# Revit family: Sink-Vanity_Top-Lavatory-KOHLER-MODERN_LIFE-K-77835T_1
name_source: partatom
category: Plumbing Fixtures
revit_build: Autodesk Revit 2017 (Build: 20160225_1515(x64)
units: mm (PartAtom-declared; Revit-internal decimal feet)

## family parameters
Cut with Voids When Loaded = No
Host = Face
OmniClass Number = 23.31.13.00
OmniClass Title = Sinks
Part Type = Normal
Room Calculation Point = No
Round Connector Dimension = Use Diameter
Shared = No

## types (2) — shared parameters
ADA Compliant = No
Assembly Code = D2010400
CW Connection = No
Cold Water Inlet = Cold Water Inlet
Date Modified = 07/26/2021
Default Elevation = 36"
Description = Minglai 600 mm Integrated Basin
Drain Included = No
Finish = Kohler-Vitreous_China-0-White
HW Connection = No
Height = 7 1/8"
Hot Water Inlet = Hot Water Inlet
Length = 18 15/16"
Manufacturer = KOHLER Co.
Master Format 2014 = 22 41 16
Master Format 2014 Name = Residential Lavatories and Sinks
Material = Vitreous China
Product Documentation Link = https://files.kohler.com.cn
Product Name = MODERN LIFE
Product Page URL = https://www.kohler.com.cn
URL = http://www.kohler.com.cn
Vent Connection = No
Waste Connection = Yes
Waste Water Outlet = Waste Water Outlet
WaterSense Certified = No
Width = 23 9/16"

## per-type parameters (varying)
| type | 8 Inch Widespread Faucet Holes | Model | Single Faucet Hole | Type |
| Single Faucet Hole, 0- White | No | K-77835T-1-0 | Yes | 1 |
| 8 Inch Widespread Faucet Holes, 0-White | Yes | K-77835T-8-0 | No | 2 |

## geometry (parser evidence)
native form markers: Sweep x3
no freeform markers — native parametric forms only
